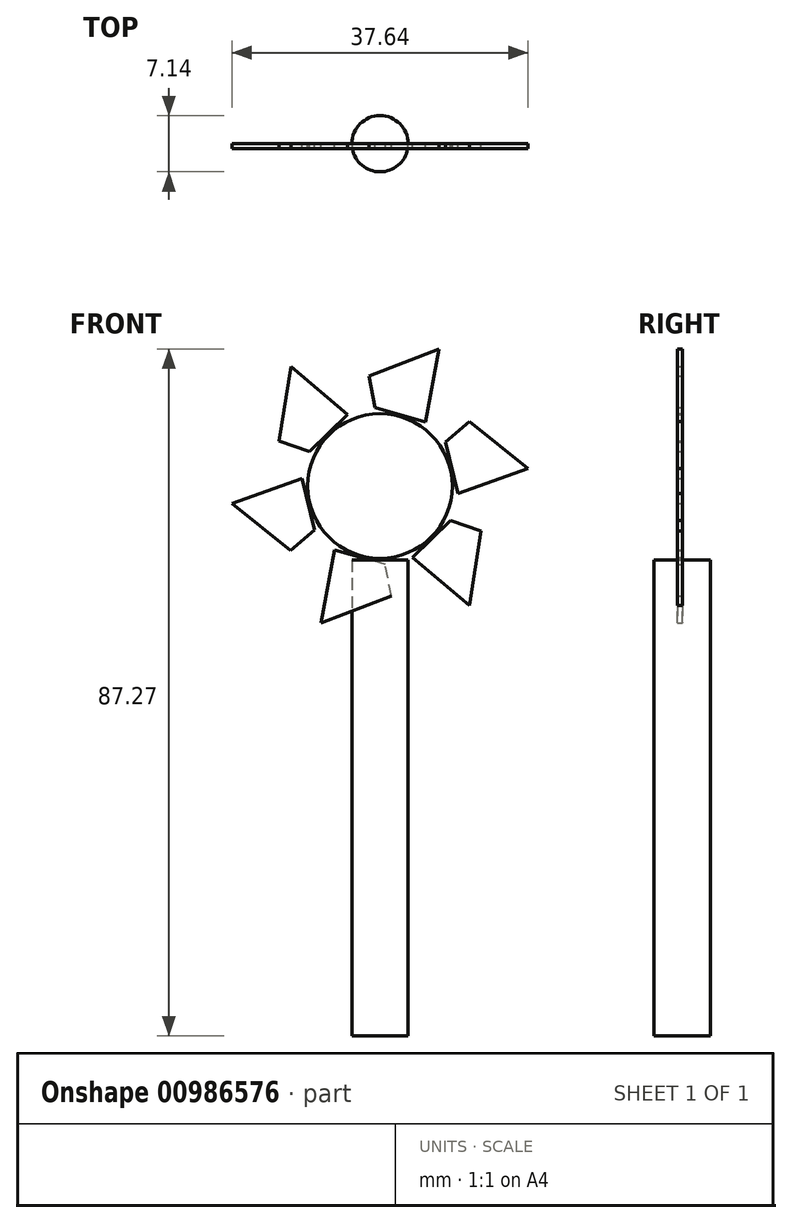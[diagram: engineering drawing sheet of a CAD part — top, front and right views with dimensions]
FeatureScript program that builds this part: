
annotation { "Feature Type Name" : "Feature", "Feature Type Description" : "" }
export const myFeature = defineFeature(function(context is Context, id is Id, definition is map)
    precondition{}
    {
        {
            var Q0;
            Q0=qCreatedBy(makeId("Top.planeOp"),FACE);
            var sketch = newSketch(context, id + "F0", { "sketchPlane" : qUnion([Q0])});
            skCircle(sketch, "E0", {"center": v(0, 0) * mm, "radius": 3.57 * mm});
            skSolve(sketch);
        }
        {
            var Q0;
            Q0=makeQuery(id+"F0.imprint","IMPRINT",FACE,{"disambiguationData":[TD([[makeQuery(id+"F0.imprint","IMPRINT",EDGE,{"derivedFrom":sQuery(id+"F0.wireOp",EDGE,"E0")}),1.0]])]});
            extrude(context, id + "F1", {"entities" : qUnion([Q0]), "depth" : 60.45 * mm, "offsetDistance" : 25.4 * mm});
        }
        {
            var Q0;
            Q0=qCreatedBy(makeId("Front.planeOp"),FACE);
            var sketch = newSketch(context, id + "F2", { "sketchPlane" : qUnion([Q0])});
            skCircle(sketch, "E1", {"center": v(0, 69.86) * mm, "radius": 9.19 * mm});
            skLineSegment(sketch, "E2", {"start": v(9.92, 68.91) * mm, "end": v(18.82, 72.08) * mm});
            skLineSegment(sketch, "E3", {"start": v(18.82, 72.08) * mm, "end": v(11.38, 78.07) * mm});
            skLineSegment(sketch, "E4", {"start": v(11.38, 78.07) * mm, "end": v(8.3, 75.42) * mm});
            skLineSegment(sketch, "E5", {"start": v(8.3, 75.42) * mm, "end": v(9.92, 68.91) * mm});
            skSolve(sketch);
        }
        {
            var Q0;
            Q0=makeQuery(id+"F2.imprint","IMPRINT",FACE,{"disambiguationData":[TD([[makeQuery(id+"F2.imprint","IMPRINT",EDGE,{"derivedFrom":sQuery(id+"F2.wireOp",EDGE,"E2")}),1.0]])]});
            var sketch = newSketch(context, id + "F3", { "sketchPlane" : qUnion([Q0])});
            skSolve(sketch);
        }
        {
            var Q0;
            Q0=makeQuery(id+"F3.imprint","IMPRINT",FACE,{"disambiguationData":[TD([[makeQuery(id+"F3.imprint","IMPRINT",EDGE,{"derivedFrom":makeQuery(id+"F2.imprint","IMPRINT",EDGE,{"derivedFrom":sQuery(id+"F2.wireOp",EDGE,"E2")})}),1.0]])]});
            var Q1;
            Q1=makeQuery(id+"F2.imprint","IMPRINT",FACE,{"disambiguationData":[TD([[makeQuery(id+"F2.imprint","IMPRINT",EDGE,{"derivedFrom":sQuery(id+"F2.wireOp",EDGE,"E1")}),1.0]])]});
            extrude(context, id + "F4", {"entities" : qUnion([Q0, Q1]), "depth" : 0.64 * mm, "offsetDistance" : 25.4 * mm});
        }
        {
            var Q0;
            Q0=makeQuery(id+"F4.opExtrude","SWEPT_BODY",BODY,{"disambiguationData":[OSD([sQuery(id+"F2.wireOp",EDGE,"E2"),sQuery(id+"F2.wireOp",EDGE,"E3"),sQuery(id+"F2.wireOp",EDGE,"E4"),sQuery(id+"F2.wireOp",EDGE,"E5")])]});
            var Q1;
            Q1=makeQuery(id+"F4.opExtrude","CAP_EDGE",EDGE,{"disambiguationData":[OSD([sQuery(id+"F2.wireOp",EDGE,"E1")])],"isStart":false});
            circularPattern(context, id + "F5", {"entities" : qUnion([Q0]), "axis" : qUnion([Q1]), "angle" : 360 * degree, "instanceCount" : 6, "equalSpace" : true});
        }
    });
